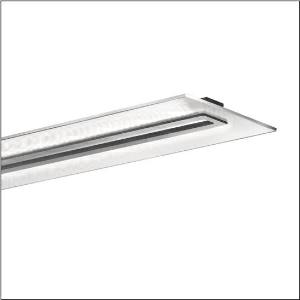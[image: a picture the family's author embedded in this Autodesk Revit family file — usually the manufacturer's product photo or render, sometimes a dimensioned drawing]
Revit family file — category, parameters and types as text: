
# Revit family: vega_r__11_5mn238dlc003_c003
name_source: partatom
category: Lighting Fixtures
units: mm (PartAtom-declared; Revit-internal decimal feet)

## family parameters
Cut with Voids When Loaded = No
Host = Face
Light Source = No
Part Type = Normal
Room Calculation Point = No
Round Connector Dimension = Use Diameter
Shared = No

## types (1)
- --- (1 x LED 3000K / CRI = 80 (unbekannt), 4300 lm, 3000K)
    Apparent Load = 35 VA
    CIE Flux Codes = 61 86 97 62 100
    Color Rendering = 80
    Color Temperature = 3000K
    Default Elevation = 1800 mm
    Description = Vega® 11, office luminaire, primary light control with prismatic reflector, of PMMA, transparent prismatic structure, CAT 2 (L<= 1500cd/m²), light emission: direct/indirect distribution, primary light characteristic: symmetric, installation type: suspended mounting, surface-mounted, LED, rated luminous flux: 4.300lm, luminous efficacy: 123lm/W, light colour: 830, colour temperature: 3000K, control gear: ECG, with terminal, 3+2-pole, max. 2.5mm², mains connection: 230V, AC, 50Hz, connection cable inclusive, cable length: 1,5m, rated input power: 35W, luminaire housing, rectangular, rounded, of aluminium section, anodised, metallic grey (RAL 9006), length: 1.250mm, width: 350mm, height: 43mm, luminaire housing, lower part, of aluminium section, anodised, metallic grey (RAL 9006), of PC, grey, protection rating (complete): IP20, insulation class (complete): insulation class I (protective earthing), certification: CE, standard: EN 50419, packaging unit: 1 piece
    Height = 40 mm  [stored 0.131234 ft]
    Lamp = 1 x LED 3000K / CRI >= 80 (unbekannt)
    Lamp Light Flux = 4300 lm
    Lamp count = 1
    Length = 1250 mm
    Luminous efficacy = 123 lm/W
    Manufacturer = Siteco
    ModVariant = No
    Model = 5MN238DLC003
    Mounting Place = Ceiling
    Mounting Type = Pendant
    Number of Poles = 1
    OnlyDefault = Yes
    Power Factor = 1
    Product Name = Vega® 11
    Product group = office luminaire | ceiling pendant
    ProductGroupID = 902
    Protection Class = Protection class I
    Protection Degree = IP 20
    RLX_Detail_Level = 1
    RLX_Emergency_Light_Flux = 0 lm
    RLX_Emergency_Type = 0
    RLX_Emergency_Type_DB = No
    RlxData = <blob elided: 62713 chars, md5=5a44f62d>
    Socket = socket
    Standby Power = 0 W
    System Light Flux = 4300 lm
    System Power = 35 W
    Type Comments = factory setting: luminous flux: 100 % | dim-lin: 254 | 260 mA
    Type Image = l_1004807.jpg
    URL = http://relux.com
    VarID = @adj_149837
    Voltage = 0 V
    Weight = 0.00 kg
    Width = 350 mm

note: [stored X ft] marks values corroborated as IEEE doubles in the binary element streams (Revit-internal decimal feet)

## geometry (parser evidence)
native form markers: Blend x4, Sweep x11
no freeform markers — native parametric forms only
